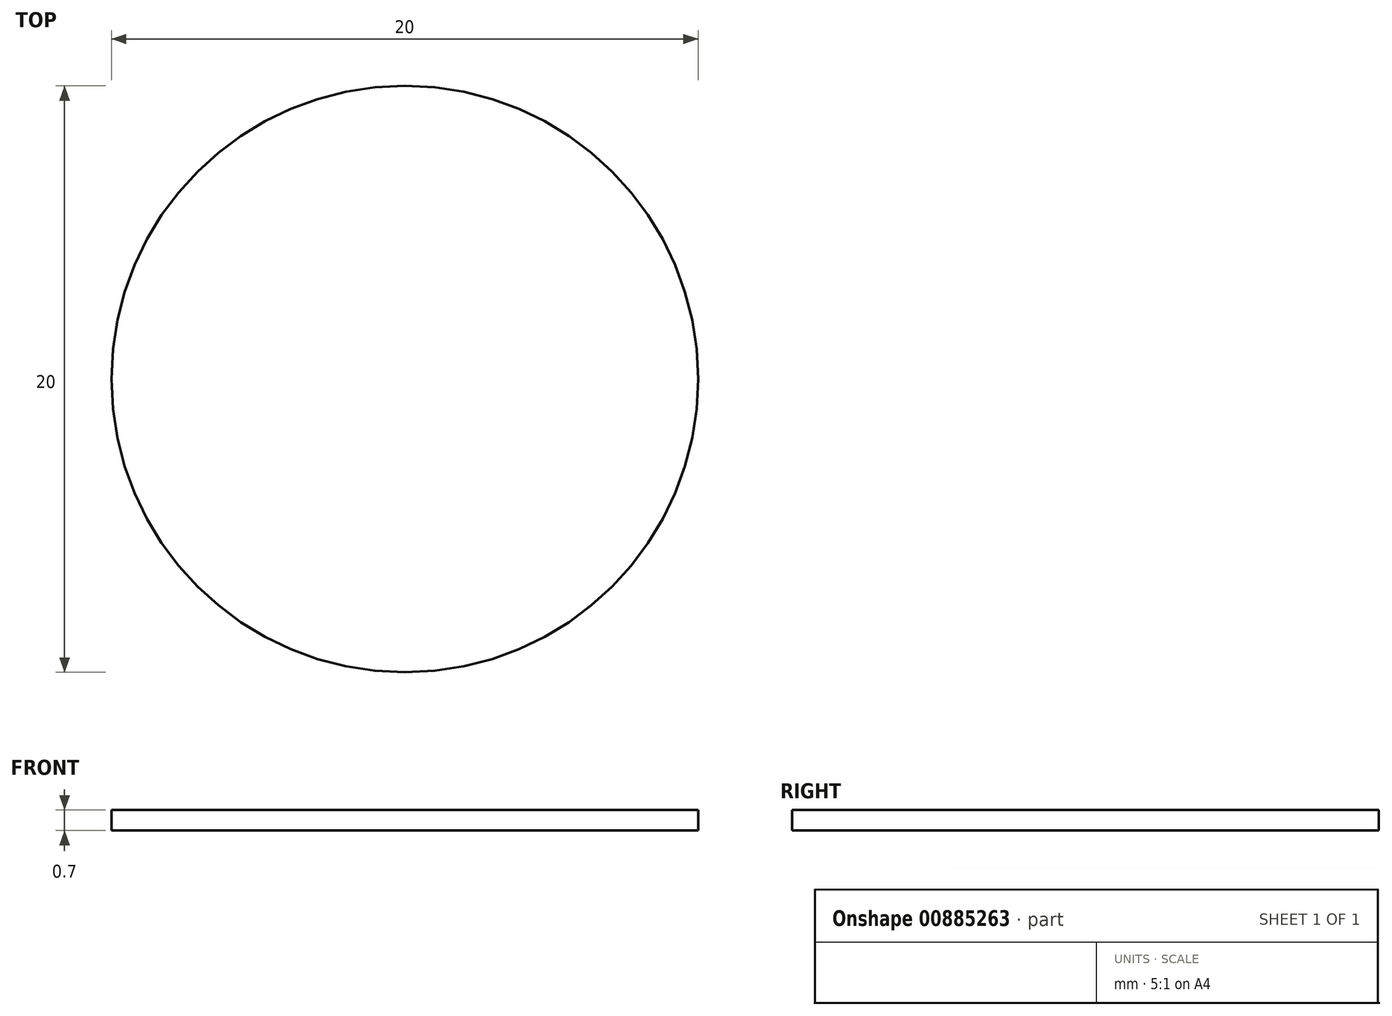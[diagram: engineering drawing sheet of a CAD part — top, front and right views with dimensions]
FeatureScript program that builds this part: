
annotation { "Feature Type Name" : "Feature", "Feature Type Description" : "" }
export const myFeature = defineFeature(function(context is Context, id is Id, definition is map)
    precondition{}
    {
        {
            var Q0;
            Q0=qCreatedBy(makeId("Top.planeOp"),FACE);
            var sketch = newSketch(context, id + "F0", { "sketchPlane" : qUnion([Q0])});
            skCircle(sketch, "E0", {"center": v(0, 0) * mm, "radius": 10 * mm});
            skSolve(sketch);
        }
        {
            var Q0;
            Q0=makeQuery(id+"F0.imprint","IMPRINT",FACE,{"disambiguationData":[TD([[makeQuery(id+"F0.imprint","IMPRINT",EDGE,{"derivedFrom":sQuery(id+"F0.wireOp",EDGE,"E0")}),1.0]])]});
            extrude(context, id + "F1", {"entities" : qUnion([Q0]), "depth" : 0.7 * mm, "offsetDistance" : 25 * mm});
        }
    });
